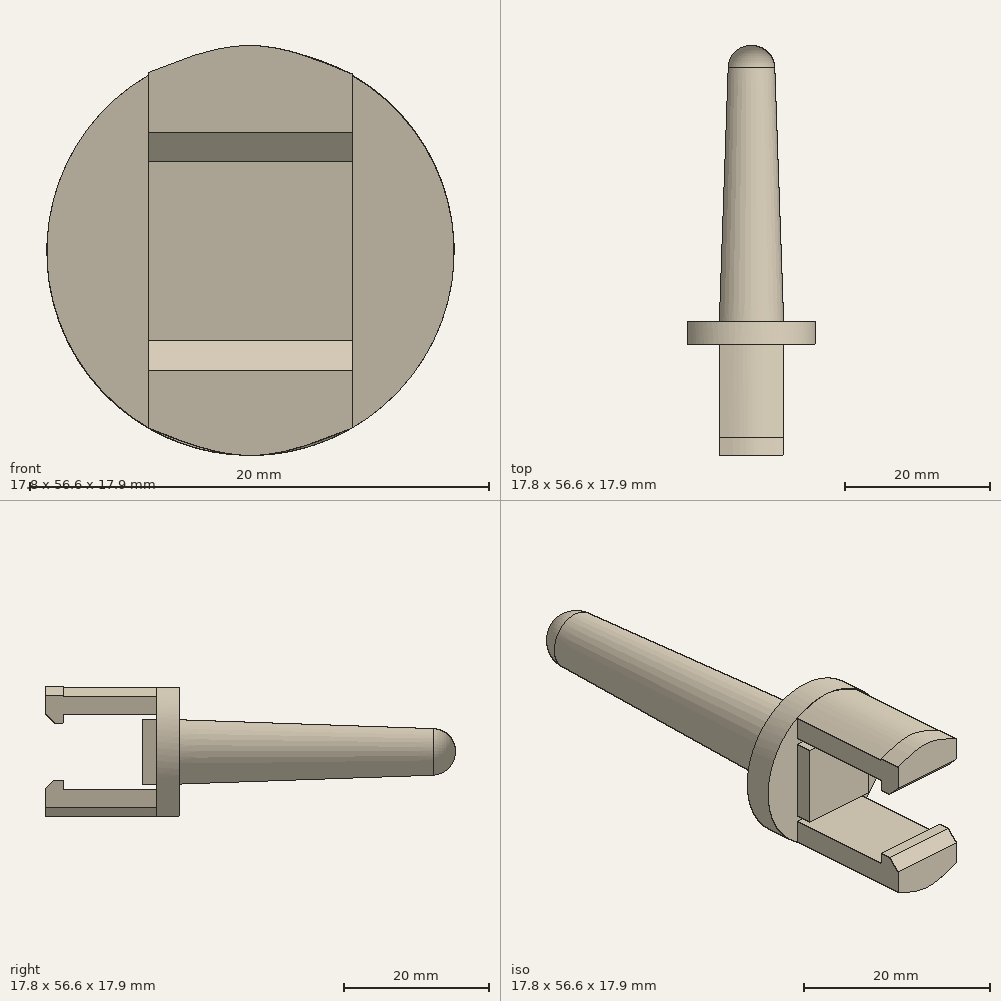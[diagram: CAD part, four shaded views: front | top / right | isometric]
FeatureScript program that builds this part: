
annotation { "Feature Type Name" : "Feature", "Feature Type Description" : "" }
export const myFeature = defineFeature(function(context is Context, id is Id, definition is map)
    precondition{}
    {
        {
            var Q0;
            Q0=qCreatedBy(makeId("Front.planeOp"),FACE);
            var sketch = newSketch(context, id + "F0", { "sketchPlane" : qUnion([Q0])});
            skCircle(sketch, "E0", {"center": v(0, 0) * mm, "radius": 8.9 * mm});
            skLineSegment(sketch, "E1.bottom", {"start": v(4.45, -4.44) * mm, "end": v(-4.45, -4.45) * mm});
            skLineSegment(sketch, "E1.top", {"start": v(4.45, 4.45) * mm, "end": v(-4.45, 4.44) * mm});
            skLineSegment(sketch, "E1.left", {"start": v(4.45, -4.44) * mm, "end": v(4.45, 4.45) * mm});
            skLineSegment(sketch, "E1.right", {"start": v(-4.45, -4.45) * mm, "end": v(-4.45, 4.44) * mm});
            skLineSegment(sketch, "E2", {"start": v(5.16, 4.45) * mm, "end": v(7.7, 4.45) * mm});
            skLineSegment(sketch, "E3", {"start": v(5.16, 4.45) * mm, "end": v(5.16, -4.45) * mm});
            skLineSegment(sketch, "E4", {"start": v(5.16, -4.45) * mm, "end": v(7.7, -4.45) * mm});
            skFitSpline(sketch, "E5", {"points": [v(7.7, 4.45) * mm, v(8.9, 0) * mm, v(7.7, -4.44) * mm], "startDerivative": vector(3.57, -8.9) * mm, "endDerivative": vector(-3.57, -8.89) * mm});
            skLineSegment(sketch, "E6", {"start": v(-7.7, 4.44) * mm, "end": v(-5.16, 4.44) * mm});
            skLineSegment(sketch, "E7", {"start": v(-5.16, 4.44) * mm, "end": v(-5.16, -4.45) * mm});
            skLineSegment(sketch, "E8", {"start": v(-7.7, -4.45) * mm, "end": v(-5.16, -4.45) * mm});
            skFitSpline(sketch, "E9", {"points": [v(-7.7, 4.44) * mm, v(-8.9, 0) * mm, v(-7.7, -4.45) * mm], "startDerivative": vector(-3.57, -8.89) * mm, "endDerivative": vector(3.57, -8.89) * mm});
            skSolve(sketch);
        }
        {
            var Q0;
            Q0=makeQuery(id+"F0.imprint","IMPRINT",FACE,{"disambiguationData":[TD([[makeQuery(id+"F0.imprint","IMPRINT",EDGE,{"derivedFrom":sQuery(id+"F0.wireOp",EDGE,"E1.bottom")}),-1.0]])]});
            var Q1;
            Q1=sQuery(id+"F0.wireOp",EDGE,"E0");
            extrude(context, id + "F1", {"entities" : qUnion([Q0]), "surfaceEntities" : qUnion([Q1]), "depth" : 5.08 * mm});
        }
        {
            var Q0;
            Q0 = qSketchRegion(id + "F0", true);
            extrude(context, id + "F2", {"entities" : qUnion([Q0]), "operationType" : NewBodyOperationType.ADD, "depth" : 3.17 * mm});
        }
        {
            var Q0;
            Q0=makeQuery(id+"F2.opExtrude","CAP_FACE",FACE,{"disambiguationData":[OSD([sQuery(id+"F0.wireOp",EDGE,"E0"),sQuery(id+"F0.wireOp",EDGE,"E1.bottom"),sQuery(id+"F0.wireOp",EDGE,"E1.top"),sQuery(id+"F0.wireOp",EDGE,"E1.left"),sQuery(id+"F0.wireOp",EDGE,"E1.right")])],"isStart":false});
            var sketch = newSketch(context, id + "F3", { "sketchPlane" : qUnion([Q0])});
            skLineSegment(sketch, "E10", {"start": v(4.44, 7.7) * mm, "end": v(4.44, 5.16) * mm});
            skLineSegment(sketch, "E11", {"start": v(4.44, 5.16) * mm, "end": v(-4.45, 5.16) * mm});
            skLineSegment(sketch, "E12", {"start": v(-4.45, 7.7) * mm, "end": v(-4.45, 5.16) * mm});
            skPoint(sketch, "E13", {"position": v(4.44, 7.7) * mm});
            skPoint(sketch, "E14", {"position": v(-4.45, 7.7) * mm});
            skFitSpline(sketch, "E15", {"points": [v(4.45, 7.7) * mm, v(0, 8.9) * mm, v(-4.45, 7.7) * mm], "startDerivative": vector(-8.9, 3.57) * mm, "endDerivative": vector(-8.9, -3.57) * mm});
            skLineSegment(sketch, "E16", {"start": v(4.45, -5.16) * mm, "end": v(4.45, -7.7) * mm});
            skLineSegment(sketch, "E17", {"start": v(4.45, -5.16) * mm, "end": v(-4.45, -5.16) * mm});
            skLineSegment(sketch, "E18", {"start": v(-4.45, -7.7) * mm, "end": v(-4.45, -5.16) * mm});
            skFitSpline(sketch, "E19", {"points": [v(4.45, -7.7) * mm, v(0, -8.9) * mm, v(-4.45, -7.7) * mm], "startDerivative": vector(-8.9, -3.57) * mm, "endDerivative": vector(-8.89, 3.57) * mm});
            skSolve(sketch);
        }
        {
            var Q0;
            Q0 = qSketchRegion(id + "F3", true);
            extrude(context, id + "F4", {"entities" : qUnion([Q0]), "operationType" : NewBodyOperationType.ADD, "depth" : 12.78 * mm});
        }
        {
            var Q0;
            {var subQ0=sQuery(id+"F0.wireOp",EDGE,"E1.right");var subQ1=sQuery(id+"F0.wireOp",EDGE,"E1.left");var subQ2=sQuery(id+"F0.wireOp",EDGE,"E1.top");var subQ3=sQuery(id+"F0.wireOp",EDGE,"E1.bottom");Q0=makeQuery(id+"F2.boolean.opBoolean","MERGE",FACE,{"derivedFrom":[makeQuery(id+"F1.opExtrude","CAP_FACE",FACE,{"disambiguationData":[OSD([subQ3,subQ2,subQ1,subQ0])],"isStart":true}),makeQuery(id+"F2.opExtrude","CAP_FACE",FACE,{"disambiguationData":[OSD([sQuery(id+"F0.wireOp",EDGE,"E0"),subQ3,subQ2,subQ1,subQ0])],"isStart":true})]});}
            var sketch = newSketch(context, id + "F5", { "sketchPlane" : qUnion([Q0])});
            skCircle(sketch, "E20", {"center": v(0, 0) * mm, "radius": 4.44 * mm});
            skSolve(sketch);
        }
        {
            var Q0;
            Q0=makeQuery(id+"F5.imprint","IMPRINT",FACE,{"disambiguationData":[TD([[makeQuery(id+"F5.imprint","IMPRINT",EDGE,{"derivedFrom":sQuery(id+"F5.wireOp",EDGE,"E20")}),1.0]])]});
            var Q1;
            Q1=sQuery(id+"F5.wireOp",EDGE,"E20");
            extrude(context, id + "F6", {"entities" : qUnion([Q0]), "operationType" : NewBodyOperationType.ADD, "surfaceEntities" : qUnion([Q1]), "depth" : 38.1 * mm, "hasDraft" : true, "draftAngle" : 2 * degree, "draftPullDirection" : true, "hasSecondDirection" : true, "secondDirectionBound" : SecondDirectionBoundingType.UP_TO_NEXT, "secondDirectionOppositeDirection" : true, "secondDirectionDepth" : 6.35 * mm});
        }
        {
            var Q0;
            Q0=makeQuery(id+"F6.opExtrude","CAP_EDGE",EDGE,{"disambiguationData":[OSD([sQuery(id+"F5.wireOp",EDGE,"E20")])],"isStart":false});
            fillet(context, id + "F7", {"entities" : qUnion([Q0]), "radius" : 3.17 * mm, "tangentPropagation" : true, "allowEdgeOverflow" : false});
        }
        {
            var Q0;
            Q0=makeQuery(id+"F4.opExtrude","CAP_FACE",FACE,{"disambiguationData":[OSD([sQuery(id+"F3.wireOp",EDGE,"E16"),sQuery(id+"F3.wireOp",EDGE,"E17"),sQuery(id+"F3.wireOp",EDGE,"E18"),sQuery(id+"F3.wireOp",EDGE,"E19")])],"isStart":false});
            var sketch = newSketch(context, id + "F8", { "sketchPlane" : qUnion([Q0])});
            skLineSegment(sketch, "E21", {"start": v(-4.45, -7.7) * mm, "end": v(-4.45, -3.89) * mm});
            skLineSegment(sketch, "E22", {"start": v(-4.45, -3.89) * mm, "end": v(4.45, -3.89) * mm});
            skLineSegment(sketch, "E23", {"start": v(4.45, -3.89) * mm, "end": v(4.45, -7.7) * mm});
            skFitSpline(sketch, "E24", {"points": [v(-4.45, -7.7) * mm, v(0, -8.9) * mm, v(4.45, -7.7) * mm], "startDerivative": vector(8.9, -3.57) * mm, "endDerivative": vector(8.89, 3.57) * mm});
            skLineSegment(sketch, "E25", {"start": v(-4.45, 7.82) * mm, "end": v(-4.45, 3.95) * mm});
            skLineSegment(sketch, "E26", {"start": v(-4.45, 3.95) * mm, "end": v(-4.45, 7.76) * mm});
            skLineSegment(sketch, "E27", {"start": v(-4.45, 3.95) * mm, "end": v(4.45, 3.95) * mm});
            skLineSegment(sketch, "E28", {"start": v(4.45, 7.76) * mm, "end": v(4.45, 3.95) * mm});
            skFitSpline(sketch, "E29", {"points": [v(-4.45, 7.82) * mm, v(0, 9) * mm, v(4.45, 7.76) * mm], "startDerivative": vector(8.9, 3.58) * mm, "endDerivative": vector(8.88, -3.71) * mm});
            skSolve(sketch);
        }
        {
            var Q0;
            Q0 = qSketchRegion(id + "F8", true);
            extrude(context, id + "F9", {"entities" : qUnion([Q0]), "operationType" : NewBodyOperationType.ADD, "depth" : 2.54 * mm});
        }
        {
            var Q0;
            Q0=makeQuery(id+"F9.opExtrude","CAP_EDGE",EDGE,{"disambiguationData":[OSD([sQuery(id+"F8.wireOp",EDGE,"E27")])],"isStart":false});
            fillet(context, id + "F10", {"entities" : qUnion([Q0]), "radius" : 1.27 * mm, "tangentPropagation" : true, "rho" : 0, "crossSection" : FilletCrossSection.CONIC, "allowEdgeOverflow" : false});
        }
        {
            var Q0;
            Q0=makeQuery(id+"F9.opExtrude","CAP_EDGE",EDGE,{"disambiguationData":[OSD([sQuery(id+"F8.wireOp",EDGE,"E22")])],"isStart":false});
            fillet(context, id + "F11", {"entities" : qUnion([Q0]), "radius" : 1.27 * mm, "tangentPropagation" : true, "rho" : 0, "crossSection" : FilletCrossSection.CONIC, "allowEdgeOverflow" : false});
        }
    });
